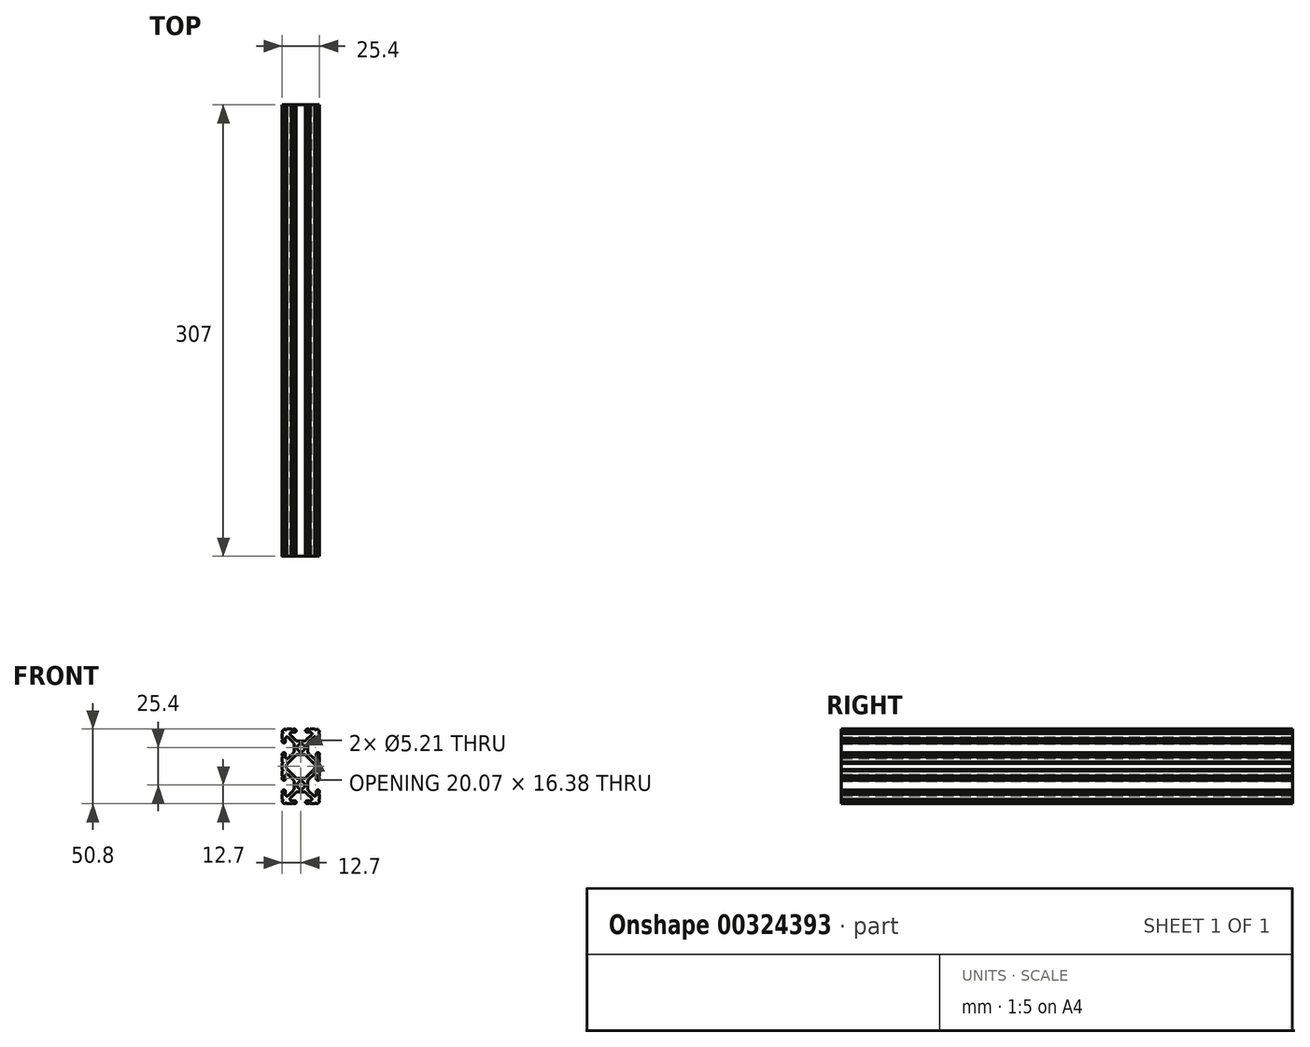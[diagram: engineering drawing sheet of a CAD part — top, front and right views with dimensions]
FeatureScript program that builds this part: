
annotation { "Feature Type Name" : "Feature", "Feature Type Description" : "" }
export const myFeature = defineFeature(function(context is Context, id is Id, definition is map)
    precondition{}
    {
        {
            var Q0;
            Q0=qCreatedBy(makeId("Front.planeOp"),FACE);
            var sketch = newSketch(context, id + "F0", { "sketchPlane" : qUnion([Q0])});
            skArc(sketch, "E0", {"start": v(2.6, -12.7) * mm, "mid": v(0, -10.1) * mm, "end": v(-2.6, -12.7) * mm});
            skArc(sketch, "E1", {"start": v(-2.6, -12.7) * mm, "mid": v(0, -15.3) * mm, "end": v(2.6, -12.7) * mm});
            skArc(sketch, "E2", {"start": v(-12.7, 22.25) * mm, "mid": v(-12.2, 22.76) * mm, "end": v(-12.7, 23.28) * mm});
            skLineSegment(sketch, "E3", {"start": v(-12.7, 22.25) * mm, "end": v(-12.7, 19.02) * mm});
            skArc(sketch, "E4", {"start": v(-12.7, 18) * mm, "mid": v(-12.2, 18.52) * mm, "end": v(-12.7, 19.02) * mm});
            skLineSegment(sketch, "E5", {"start": v(-12.7, 18) * mm, "end": v(-12.7, 17) * mm});
            skArc(sketch, "E6", {"start": v(-12.7, 17) * mm, "mid": v(-11.6, 15.9) * mm, "end": v(-10.5, 17) * mm});
            skLineSegment(sketch, "E7", {"start": v(-10.5, 17) * mm, "end": v(-10.5, 19.17) * mm});
            skArc(sketch, "E8", {"start": v(-8.76, 19.9) * mm, "mid": v(-9.86, 20.11) * mm, "end": v(-10.5, 19.17) * mm});
            skLineSegment(sketch, "E9", {"start": v(-8.76, 19.9) * mm, "end": v(-5.44, 16.58) * mm});
            skArc(sketch, "E10", {"start": v(-4.5, 14.33) * mm, "mid": v(-4.75, 15.55) * mm, "end": v(-5.44, 16.58) * mm});
            skLineSegment(sketch, "E11", {"start": v(-4.5, 14.33) * mm, "end": v(-4.5, 11.07) * mm});
            skArc(sketch, "E12", {"start": v(-5.44, 8.82) * mm, "mid": v(-4.75, 9.85) * mm, "end": v(-4.5, 11.07) * mm});
            skLineSegment(sketch, "E13", {"start": v(-5.44, 8.82) * mm, "end": v(-8.76, 5.5) * mm});
            skArc(sketch, "E14", {"start": v(-10.5, 6.23) * mm, "mid": v(-9.86, 5.29) * mm, "end": v(-8.76, 5.5) * mm});
            skLineSegment(sketch, "E15", {"start": v(-10.5, 6.23) * mm, "end": v(-10.5, 8.4) * mm});
            skArc(sketch, "E16", {"start": v(-10.5, 8.4) * mm, "mid": v(-11.6, 9.5) * mm, "end": v(-12.7, 8.4) * mm});
            skLineSegment(sketch, "E17", {"start": v(-12.7, 8.4) * mm, "end": v(-12.7, 7.4) * mm});
            skArc(sketch, "E18", {"start": v(-12.7, 6.38) * mm, "mid": v(-12.2, 6.88) * mm, "end": v(-12.7, 7.4) * mm});
            skLineSegment(sketch, "E19", {"start": v(-12.7, 6.38) * mm, "end": v(-12.7, 3.15) * mm});
            skArc(sketch, "E20", {"start": v(-12.7, 2.13) * mm, "mid": v(-12.2, 2.64) * mm, "end": v(-12.7, 3.15) * mm});
            skLineSegment(sketch, "E21", {"start": v(-12.7, 2.13) * mm, "end": v(-12.7, -2.13) * mm});
            skArc(sketch, "E22", {"start": v(-12.7, -3.15) * mm, "mid": v(-12.2, -2.64) * mm, "end": v(-12.7, -2.13) * mm});
            skLineSegment(sketch, "E23", {"start": v(-12.7, -3.15) * mm, "end": v(-12.7, -6.38) * mm});
            skArc(sketch, "E24", {"start": v(-12.7, -7.4) * mm, "mid": v(-12.2, -6.88) * mm, "end": v(-12.7, -6.38) * mm});
            skLineSegment(sketch, "E25", {"start": v(-12.7, -7.4) * mm, "end": v(-12.7, -8.4) * mm});
            skArc(sketch, "E26", {"start": v(-12.7, -8.4) * mm, "mid": v(-11.6, -9.5) * mm, "end": v(-10.5, -8.4) * mm});
            skLineSegment(sketch, "E27", {"start": v(-10.5, -8.4) * mm, "end": v(-10.5, -6.23) * mm});
            skArc(sketch, "E28", {"start": v(-8.76, -5.5) * mm, "mid": v(-9.86, -5.29) * mm, "end": v(-10.5, -6.23) * mm});
            skLineSegment(sketch, "E29", {"start": v(-8.76, -5.5) * mm, "end": v(-5.44, -8.82) * mm});
            skArc(sketch, "E30", {"start": v(-4.5, -11.07) * mm, "mid": v(-4.75, -9.85) * mm, "end": v(-5.44, -8.82) * mm});
            skLineSegment(sketch, "E31", {"start": v(-4.5, -11.07) * mm, "end": v(-4.5, -14.33) * mm});
            skArc(sketch, "E32", {"start": v(-5.44, -16.58) * mm, "mid": v(-4.75, -15.55) * mm, "end": v(-4.5, -14.33) * mm});
            skLineSegment(sketch, "E33", {"start": v(-5.44, -16.58) * mm, "end": v(-8.76, -19.9) * mm});
            skArc(sketch, "E34", {"start": v(-10.5, -19.17) * mm, "mid": v(-9.86, -20.11) * mm, "end": v(-8.76, -19.9) * mm});
            skLineSegment(sketch, "E35", {"start": v(-10.5, -19.17) * mm, "end": v(-10.5, -17) * mm});
            skArc(sketch, "E36", {"start": v(-10.5, -17) * mm, "mid": v(-11.6, -15.9) * mm, "end": v(-12.7, -17) * mm});
            skLineSegment(sketch, "E37", {"start": v(-12.7, -17) * mm, "end": v(-12.7, -18) * mm});
            skArc(sketch, "E38", {"start": v(-12.7, -19.02) * mm, "mid": v(-12.2, -18.52) * mm, "end": v(-12.7, -18) * mm});
            skLineSegment(sketch, "E39", {"start": v(-12.7, -19.02) * mm, "end": v(-12.7, -22.25) * mm});
            skArc(sketch, "E40", {"start": v(-12.7, -23.28) * mm, "mid": v(-12.2, -22.76) * mm, "end": v(-12.7, -22.25) * mm});
            skArc(sketch, "E41", {"start": v(-12.7, -23.28) * mm, "mid": v(-12.08, -24.78) * mm, "end": v(-10.58, -25.4) * mm});
            skArc(sketch, "E42", {"start": v(-9.55, -25.4) * mm, "mid": v(-10.06, -24.9) * mm, "end": v(-10.58, -25.4) * mm});
            skLineSegment(sketch, "E43", {"start": v(-9.55, -25.4) * mm, "end": v(-6.32, -25.4) * mm});
            skArc(sketch, "E44", {"start": v(-5.3, -25.4) * mm, "mid": v(-5.82, -24.9) * mm, "end": v(-6.32, -25.4) * mm});
            skLineSegment(sketch, "E45", {"start": v(-5.3, -25.4) * mm, "end": v(-4.3, -25.4) * mm});
            skArc(sketch, "E46", {"start": v(-4.3, -25.4) * mm, "mid": v(-3.2, -24.3) * mm, "end": v(-4.3, -23.2) * mm});
            skLineSegment(sketch, "E47", {"start": v(-4.3, -23.2) * mm, "end": v(-6.47, -23.2) * mm});
            skArc(sketch, "E48", {"start": v(-7.2, -21.46) * mm, "mid": v(-7.41, -22.56) * mm, "end": v(-6.47, -23.2) * mm});
            skLineSegment(sketch, "E49", {"start": v(-7.2, -21.46) * mm, "end": v(-3.88, -18.14) * mm});
            skArc(sketch, "E50", {"start": v(-1.63, -17.2) * mm, "mid": v(-2.85, -17.45) * mm, "end": v(-3.88, -18.14) * mm});
            skLineSegment(sketch, "E51", {"start": v(-1.63, -17.2) * mm, "end": v(1.63, -17.2) * mm});
            skArc(sketch, "E52", {"start": v(3.88, -18.14) * mm, "mid": v(2.85, -17.45) * mm, "end": v(1.63, -17.2) * mm});
            skLineSegment(sketch, "E53", {"start": v(3.88, -18.14) * mm, "end": v(7.2, -21.46) * mm});
            skArc(sketch, "E54", {"start": v(6.47, -23.2) * mm, "mid": v(7.41, -22.56) * mm, "end": v(7.2, -21.46) * mm});
            skLineSegment(sketch, "E55", {"start": v(6.47, -23.2) * mm, "end": v(4.3, -23.2) * mm});
            skArc(sketch, "E56", {"start": v(4.3, -23.2) * mm, "mid": v(3.2, -24.3) * mm, "end": v(4.3, -25.4) * mm});
            skLineSegment(sketch, "E57", {"start": v(4.3, -25.4) * mm, "end": v(5.3, -25.4) * mm});
            skArc(sketch, "E58", {"start": v(6.32, -25.4) * mm, "mid": v(5.82, -24.9) * mm, "end": v(5.3, -25.4) * mm});
            skLineSegment(sketch, "E59", {"start": v(6.32, -25.4) * mm, "end": v(9.55, -25.4) * mm});
            skArc(sketch, "E60", {"start": v(10.58, -25.4) * mm, "mid": v(10.06, -24.9) * mm, "end": v(9.55, -25.4) * mm});
            skArc(sketch, "E61", {"start": v(10.58, -25.4) * mm, "mid": v(12.08, -24.78) * mm, "end": v(12.7, -23.28) * mm});
            skArc(sketch, "E62", {"start": v(12.7, -22.25) * mm, "mid": v(12.2, -22.76) * mm, "end": v(12.7, -23.28) * mm});
            skLineSegment(sketch, "E63", {"start": v(12.7, -22.25) * mm, "end": v(12.7, -19.02) * mm});
            skArc(sketch, "E64", {"start": v(12.7, -18) * mm, "mid": v(12.2, -18.52) * mm, "end": v(12.7, -19.02) * mm});
            skLineSegment(sketch, "E65", {"start": v(12.7, -18) * mm, "end": v(12.7, -17) * mm});
            skArc(sketch, "E66", {"start": v(12.7, -17) * mm, "mid": v(11.6, -15.9) * mm, "end": v(10.5, -17) * mm});
            skLineSegment(sketch, "E67", {"start": v(10.5, -17) * mm, "end": v(10.5, -19.17) * mm});
            skArc(sketch, "E68", {"start": v(8.76, -19.9) * mm, "mid": v(9.86, -20.11) * mm, "end": v(10.5, -19.17) * mm});
            skLineSegment(sketch, "E69", {"start": v(8.76, -19.9) * mm, "end": v(5.44, -16.58) * mm});
            skArc(sketch, "E70", {"start": v(4.5, -14.33) * mm, "mid": v(4.75, -15.55) * mm, "end": v(5.44, -16.58) * mm});
            skLineSegment(sketch, "E71", {"start": v(4.5, -14.33) * mm, "end": v(4.5, -11.07) * mm});
            skArc(sketch, "E72", {"start": v(5.44, -8.82) * mm, "mid": v(4.75, -9.85) * mm, "end": v(4.5, -11.07) * mm});
            skLineSegment(sketch, "E73", {"start": v(5.44, -8.82) * mm, "end": v(8.76, -5.5) * mm});
            skArc(sketch, "E74", {"start": v(10.5, -6.23) * mm, "mid": v(9.86, -5.29) * mm, "end": v(8.76, -5.5) * mm});
            skLineSegment(sketch, "E75", {"start": v(10.5, -6.23) * mm, "end": v(10.5, -8.4) * mm});
            skArc(sketch, "E76", {"start": v(10.5, -8.4) * mm, "mid": v(11.6, -9.5) * mm, "end": v(12.7, -8.4) * mm});
            skLineSegment(sketch, "E77", {"start": v(12.7, -8.4) * mm, "end": v(12.7, -7.4) * mm});
            skArc(sketch, "E78", {"start": v(12.7, -6.38) * mm, "mid": v(12.2, -6.88) * mm, "end": v(12.7, -7.4) * mm});
            skLineSegment(sketch, "E79", {"start": v(12.7, -6.38) * mm, "end": v(12.7, -3.15) * mm});
            skArc(sketch, "E80", {"start": v(12.7, -2.13) * mm, "mid": v(12.2, -2.64) * mm, "end": v(12.7, -3.15) * mm});
            skLineSegment(sketch, "E81", {"start": v(12.7, -2.13) * mm, "end": v(12.7, 2.13) * mm});
            skArc(sketch, "E82", {"start": v(12.7, 3.15) * mm, "mid": v(12.2, 2.64) * mm, "end": v(12.7, 2.13) * mm});
            skLineSegment(sketch, "E83", {"start": v(12.7, 3.15) * mm, "end": v(12.7, 6.38) * mm});
            skArc(sketch, "E84", {"start": v(12.7, 7.4) * mm, "mid": v(12.2, 6.88) * mm, "end": v(12.7, 6.38) * mm});
            skLineSegment(sketch, "E85", {"start": v(12.7, 7.4) * mm, "end": v(12.7, 8.4) * mm});
            skArc(sketch, "E86", {"start": v(12.7, 8.4) * mm, "mid": v(11.6, 9.5) * mm, "end": v(10.5, 8.4) * mm});
            skLineSegment(sketch, "E87", {"start": v(10.5, 8.4) * mm, "end": v(10.5, 6.23) * mm});
            skArc(sketch, "E88", {"start": v(8.76, 5.5) * mm, "mid": v(9.86, 5.29) * mm, "end": v(10.5, 6.23) * mm});
            skLineSegment(sketch, "E89", {"start": v(8.76, 5.5) * mm, "end": v(5.44, 8.82) * mm});
            skArc(sketch, "E90", {"start": v(4.5, 11.07) * mm, "mid": v(4.75, 9.85) * mm, "end": v(5.44, 8.82) * mm});
            skLineSegment(sketch, "E91", {"start": v(4.5, 11.07) * mm, "end": v(4.5, 14.33) * mm});
            skArc(sketch, "E92", {"start": v(5.44, 16.58) * mm, "mid": v(4.75, 15.55) * mm, "end": v(4.5, 14.33) * mm});
            skLineSegment(sketch, "E93", {"start": v(5.44, 16.58) * mm, "end": v(8.76, 19.9) * mm});
            skArc(sketch, "E94", {"start": v(10.5, 19.17) * mm, "mid": v(9.86, 20.11) * mm, "end": v(8.76, 19.9) * mm});
            skLineSegment(sketch, "E95", {"start": v(10.5, 19.17) * mm, "end": v(10.5, 17) * mm});
            skArc(sketch, "E96", {"start": v(10.5, 17) * mm, "mid": v(11.6, 15.9) * mm, "end": v(12.7, 17) * mm});
            skLineSegment(sketch, "E97", {"start": v(12.7, 17) * mm, "end": v(12.7, 18) * mm});
            skArc(sketch, "E98", {"start": v(12.7, 19.02) * mm, "mid": v(12.2, 18.52) * mm, "end": v(12.7, 18) * mm});
            skLineSegment(sketch, "E99", {"start": v(12.7, 19.02) * mm, "end": v(12.7, 22.25) * mm});
            skArc(sketch, "E100", {"start": v(12.7, 23.28) * mm, "mid": v(12.2, 22.76) * mm, "end": v(12.7, 22.25) * mm});
            skArc(sketch, "E101", {"start": v(12.7, 23.28) * mm, "mid": v(12.08, 24.78) * mm, "end": v(10.58, 25.4) * mm});
            skArc(sketch, "E102", {"start": v(9.55, 25.4) * mm, "mid": v(10.06, 24.9) * mm, "end": v(10.58, 25.4) * mm});
            skLineSegment(sketch, "E103", {"start": v(9.55, 25.4) * mm, "end": v(6.32, 25.4) * mm});
            skArc(sketch, "E104", {"start": v(5.3, 25.4) * mm, "mid": v(5.82, 24.9) * mm, "end": v(6.32, 25.4) * mm});
            skLineSegment(sketch, "E105", {"start": v(5.3, 25.4) * mm, "end": v(4.3, 25.4) * mm});
            skArc(sketch, "E106", {"start": v(4.3, 25.4) * mm, "mid": v(3.2, 24.3) * mm, "end": v(4.3, 23.2) * mm});
            skLineSegment(sketch, "E107", {"start": v(4.3, 23.2) * mm, "end": v(6.47, 23.2) * mm});
            skArc(sketch, "E108", {"start": v(7.2, 21.46) * mm, "mid": v(7.41, 22.56) * mm, "end": v(6.47, 23.2) * mm});
            skLineSegment(sketch, "E109", {"start": v(7.2, 21.46) * mm, "end": v(3.88, 18.14) * mm});
            skArc(sketch, "E110", {"start": v(1.63, 17.2) * mm, "mid": v(2.85, 17.45) * mm, "end": v(3.88, 18.14) * mm});
            skLineSegment(sketch, "E111", {"start": v(1.63, 17.2) * mm, "end": v(-1.63, 17.2) * mm});
            skArc(sketch, "E112", {"start": v(-3.88, 18.14) * mm, "mid": v(-2.85, 17.45) * mm, "end": v(-1.63, 17.2) * mm});
            skLineSegment(sketch, "E113", {"start": v(-3.88, 18.14) * mm, "end": v(-7.2, 21.46) * mm});
            skArc(sketch, "E114", {"start": v(-6.47, 23.2) * mm, "mid": v(-7.41, 22.56) * mm, "end": v(-7.2, 21.46) * mm});
            skLineSegment(sketch, "E115", {"start": v(-6.47, 23.2) * mm, "end": v(-4.3, 23.2) * mm});
            skArc(sketch, "E116", {"start": v(-4.3, 23.2) * mm, "mid": v(-3.2, 24.3) * mm, "end": v(-4.3, 25.4) * mm});
            skLineSegment(sketch, "E117", {"start": v(-4.3, 25.4) * mm, "end": v(-5.3, 25.4) * mm});
            skArc(sketch, "E118", {"start": v(-6.32, 25.4) * mm, "mid": v(-5.82, 24.9) * mm, "end": v(-5.3, 25.4) * mm});
            skLineSegment(sketch, "E119", {"start": v(-6.32, 25.4) * mm, "end": v(-9.55, 25.4) * mm});
            skArc(sketch, "E120", {"start": v(-10.58, 25.4) * mm, "mid": v(-10.06, 24.9) * mm, "end": v(-9.55, 25.4) * mm});
            skArc(sketch, "E121", {"start": v(-10.58, 25.4) * mm, "mid": v(-12.08, 24.78) * mm, "end": v(-12.7, 23.28) * mm});
            skArc(sketch, "E122", {"start": v(2.6, 12.7) * mm, "mid": v(0, 15.3) * mm, "end": v(-2.6, 12.7) * mm});
            skArc(sketch, "E123", {"start": v(-2.6, 12.7) * mm, "mid": v(0, 10.1) * mm, "end": v(2.6, 12.7) * mm});
            skArc(sketch, "E124", {"start": v(-9.57, 1.57) * mm, "mid": v(-9.91, 1.05) * mm, "end": v(-10.03, 0.45) * mm});
            skLineSegment(sketch, "E125", {"start": v(-3.88, 7.26) * mm, "end": v(-9.57, 1.57) * mm});
            skArc(sketch, "E126", {"start": v(-1.63, 8.2) * mm, "mid": v(-2.85, 7.95) * mm, "end": v(-3.88, 7.26) * mm});
            skLineSegment(sketch, "E127", {"start": v(1.63, 8.2) * mm, "end": v(-1.63, 8.2) * mm});
            skArc(sketch, "E128", {"start": v(3.88, 7.26) * mm, "mid": v(2.85, 7.95) * mm, "end": v(1.63, 8.2) * mm});
            skLineSegment(sketch, "E129", {"start": v(9.57, 1.57) * mm, "end": v(3.88, 7.26) * mm});
            skArc(sketch, "E130", {"start": v(10.03, 0.45) * mm, "mid": v(9.91, 1.05) * mm, "end": v(9.57, 1.57) * mm});
            skLineSegment(sketch, "E131", {"start": v(10.03, -0.45) * mm, "end": v(10.03, 0.45) * mm});
            skArc(sketch, "E132", {"start": v(9.57, -1.57) * mm, "mid": v(9.91, -1.05) * mm, "end": v(10.03, -0.45) * mm});
            skLineSegment(sketch, "E133", {"start": v(3.88, -7.26) * mm, "end": v(9.57, -1.57) * mm});
            skArc(sketch, "E134", {"start": v(1.63, -8.2) * mm, "mid": v(2.85, -7.95) * mm, "end": v(3.88, -7.26) * mm});
            skLineSegment(sketch, "E135", {"start": v(-1.63, -8.2) * mm, "end": v(1.63, -8.2) * mm});
            skArc(sketch, "E136", {"start": v(-3.88, -7.26) * mm, "mid": v(-2.85, -7.95) * mm, "end": v(-1.63, -8.2) * mm});
            skLineSegment(sketch, "E137", {"start": v(-9.57, -1.57) * mm, "end": v(-3.88, -7.26) * mm});
            skArc(sketch, "E138", {"start": v(-10.03, -0.45) * mm, "mid": v(-9.91, -1.05) * mm, "end": v(-9.57, -1.57) * mm});
            skLineSegment(sketch, "E139", {"start": v(-10.03, 0.45) * mm, "end": v(-10.03, -0.45) * mm});
            skSolve(sketch);
        }
        {
            var Q0;
            Q0=makeQuery(id+"F0.imprint","IMPRINT",FACE,{"disambiguationData":[TD([[makeQuery(id+"F0.imprint","IMPRINT",EDGE,{"derivedFrom":sQuery(id+"F0.wireOp",EDGE,"E0")}),-1.0]])]});
            extrude(context, id + "F1", {"entities" : qUnion([Q0]), "depth" : 307 * mm});
        }
    });
